# Revit family: 98QMT,QBT_231217_1
name_source: partatom
category: 통신 장치
units: mm (PartAtom-declared; Revit-internal decimal feet)

## family parameters
OmniClass 번호 = 23.85.10.14.24
OmniClass 제목 = Video Monitors
공유 = 아니오
로드될 때 보이드를 사용하여 절단 = 아니오
룸 계산 점 = 아니오
부품 유형 = 보통
원형 커넥터 치수 = 지름 사용
작업 기준면 기반 = 아니오
주석 방향을 유지합니다. = 아니오
항상 수직 = 예

## types (2) — shared parameters
Active Display Area = 2158.848(H) x 1214.352(V)
Bezel Width (mm) = 17.9
Color Gamut = 72%
Contrast Ratio (Typ.) = 1200:1
Diagonal Size (Class) = 98  [stored 0.321522 ft]
Diagonal Size (Measured) = 97.5
Dimension Package (mm) = 2369 x 1405 x 350
Dimension Set (mm) = 2195.8 x 1250.8 x 96.5
Dimension Set Depth (mm) = 96.5  [stored 0.316601 ft]
Dimension Set Height (mm) = 1250.8  [stored 4.10367 ft]
Dimension Set Width (mm) = 2195.8  [stored 7.20407 ft]
Display Colors = 16.7M(True Display) 1.07B(Ditherd 10bit)
Dynamic C/R = MEGA
EMC = Class A
External Control = RS232C(in/out) thru stereo jack, RJ45
External Sensor = IR
H-Scanning Frequency = 30 ~ 81kHZ
Haze = 25%
Input Audio = Stereo mini Jack, DVI, HDMI
Input HDCP = HDCP2.2
Input RGB = DVI-D, Display Port 1.2 (1)
Input USB = USB 2.0 x 2
Input Video = HDMI 2.0 (2)
Internal Clock Speed = 1.7GHz
Internal Graphics = Graphic resolution : 1920x1080 Output resolution : 1920x1080 (Scale up from graphic processing result.)
Internal IO Ports = USB 2.0
Internal Main Memory Interface = 2.5GB, LPDDR4 1.5GHz 64bit
Internal Multimedia = Video Decoder  : MPEG-1/2/4, H.263, H.264/AVC, UHD H.264/AVC,  VC-1, AVS+, HEVC, JPEG, PNG, VP8, VP9  *Audio Decoder : AC3 (DD), MPEG
Internal On-Chip Cache Memory = L1 Instruction Cache : 48KB L1 Data Cache : 32KB L2 Cache : 2MB
Internal Operating System = Tizen 4.0 (VDLinux)
Internal Processor = Cortex A72 1.7GHz Quad-Core CPU
Internal Storage (FDM) = 8GB (3.88GB Occupied by O/S, 4.12GB Available)
Key = UHD Signage Display Slim & Light Signage with Built-in MagicInfo S6, SSSP 6.0
Maximum Pixel Frequency = 594MHz
Operation Hour = 24/7
Optional Mount = WMN8200SG (Land Only)
Optional Specialty = -
Optional Stand = -
Orientation = Landscape / Portrait
Output Audio = Stereo mini Jack
Output RGB = HDMI 2.0 (Loop-out)
Pixel Pitch (mm) = 0.562 x 0.562 (mm)
Power Consumption Sleep mode = 0.5
Power Supply = AC100 - 240V, 50/60 Hz
Power Type = Internal
Relative Humidity = 10~80%
Resolution = UHD (3840 x 2160)
Response Time (GtoG) = 8ms
Safety = 60950-1
Screen = Samsung Electronics Screen
Security = 802.1 x (WPA2 Enterprise) : EAP-TLS, EAP-TTLS, EAP-PEAP
Sound = Built in Speaker(10W + 10W)
Temperature = 0℃ ~ 40℃
Type = Direct LED BLU
V-Scanning Frequency = 48 ~ 75HZ
VESA Mount = 800 x 400
Viewing Angle(H/V) = 178/178
Weight Package (kg) = 106
Weight Set (kg) = 83
제조업체 = Samsung Electronics Co., Ltd.
조합 코드 = E1020500
키노트 = 11 52 00

## per-type parameters (varying)
| type | Brightness (Typ.) | Power Consumption BTU(Max) | Power Consumption Max [W/h] | Power Consumption Rating [W/h] | Power Consumption Typical [W/h] |
| UHD Signage QM98T | 500 | 2101.9 | 616 | 560 | 414 |
| UHD Signage QB98T | 350 | 1576.4 | 492 | 420 | 360 |

note: column(s) folded — value = type name in every type: 모델

note: [stored X ft] marks values corroborated as IEEE doubles in the binary element streams (Revit-internal decimal feet)
